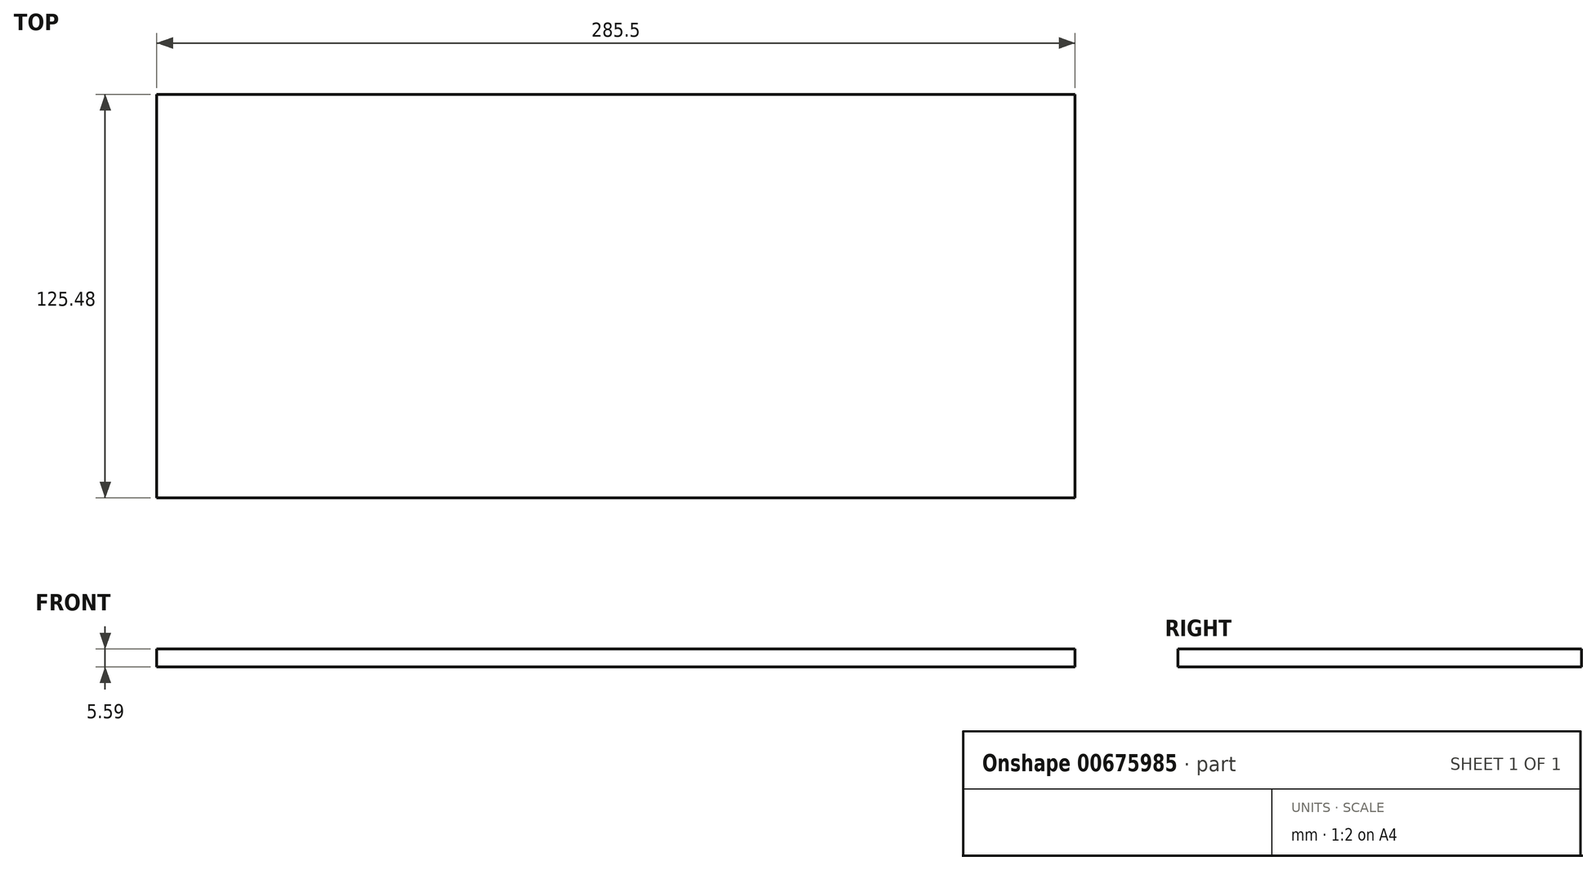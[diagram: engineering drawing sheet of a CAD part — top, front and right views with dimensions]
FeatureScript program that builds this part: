
annotation { "Feature Type Name" : "Feature", "Feature Type Description" : "" }
export const myFeature = defineFeature(function(context is Context, id is Id, definition is map)
    precondition{}
    {
        {
            var Q0;
            Q0=qCreatedBy(makeId("Top.planeOp"),FACE);
            var sketch = newSketch(context, id + "F0", { "sketchPlane" : qUnion([Q0])});
            skLineSegment(sketch, "E0.bottom", {"start": v(-142.75, 62.74) * mm, "end": v(142.75, 62.74) * mm});
            skLineSegment(sketch, "E0.top", {"start": v(-142.75, -62.74) * mm, "end": v(142.75, -62.74) * mm});
            skLineSegment(sketch, "E0.left", {"start": v(-142.75, 62.74) * mm, "end": v(-142.75, -62.74) * mm});
            skLineSegment(sketch, "E0.right", {"start": v(142.75, 62.74) * mm, "end": v(142.75, -62.74) * mm});
            skPoint(sketch, "E0.middle", {"position": v(0, 0) * mm});
            skSolve(sketch);
        }
        {
            var Q0;
            Q0 = qSketchRegion(id + "F0", true);
            extrude(context, id + "F1", {"entities" : qUnion([Q0]), "depth" : 5.6 * mm, "offsetDistance" : 25.4 * mm});
        }
    });
